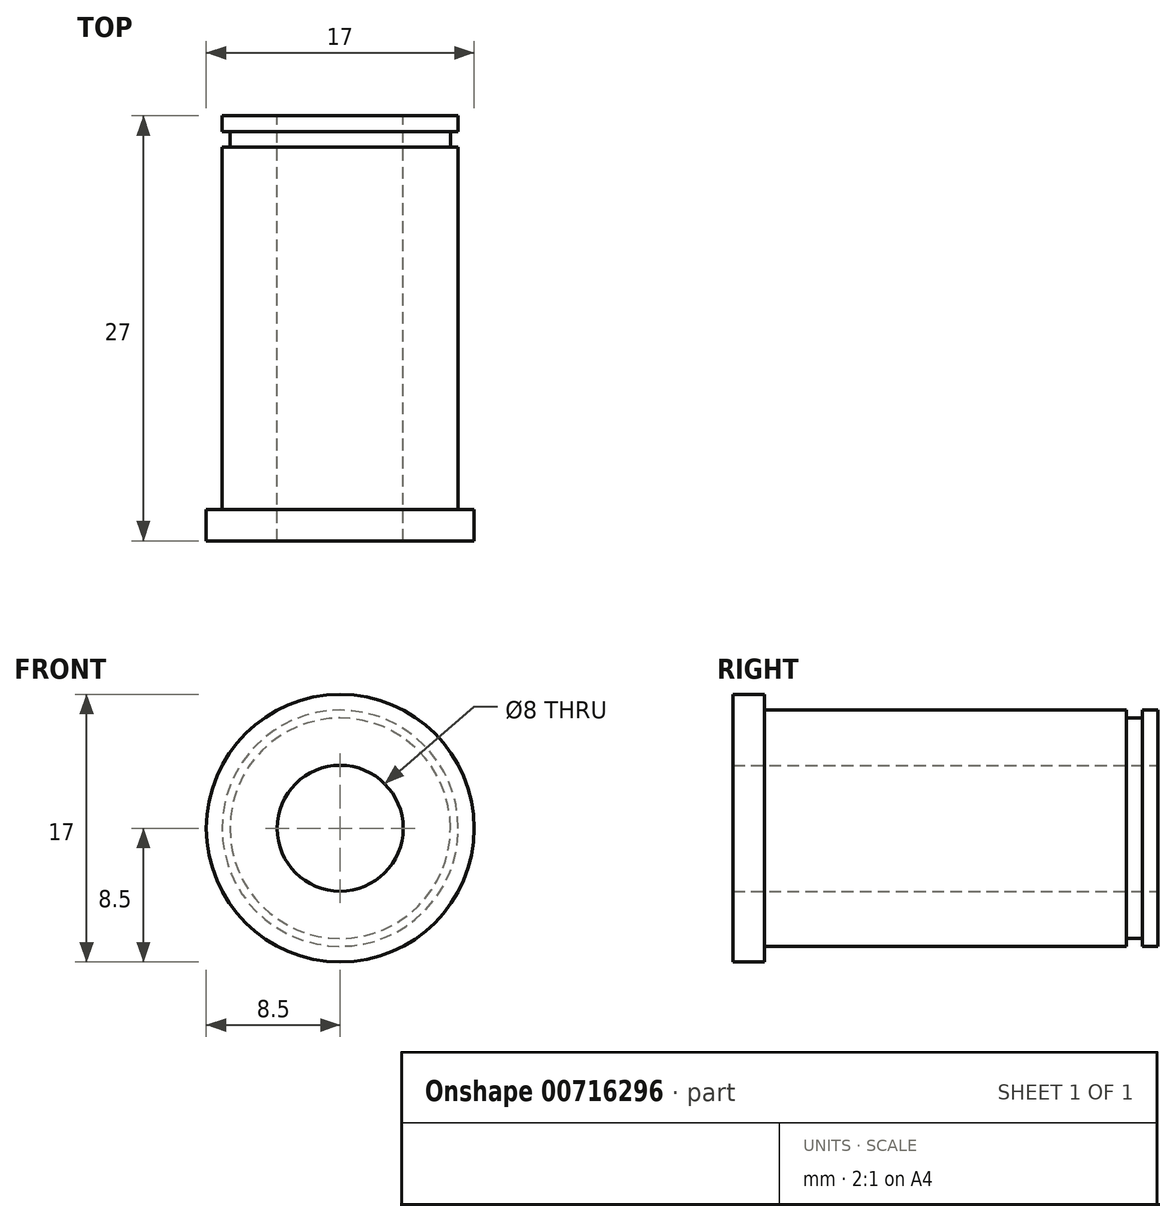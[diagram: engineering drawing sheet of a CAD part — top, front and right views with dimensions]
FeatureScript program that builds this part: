
annotation { "Feature Type Name" : "Feature", "Feature Type Description" : "" }
export const myFeature = defineFeature(function(context is Context, id is Id, definition is map)
    precondition{}
    {
        {
            var Q0;
            Q0=qCreatedBy(makeId("Front.planeOp"),FACE);
            var sketch = newSketch(context, id + "F0", { "sketchPlane" : qUnion([Q0])});
            skCircle(sketch, "E0", {"center": v(0, 0) * mm, "radius": 7.5 * mm});
            skCircle(sketch, "E1", {"center": v(0, 0) * mm, "radius": 8.5 * mm});
            skCircle(sketch, "E2", {"center": v(0, 0) * mm, "radius": 7 * mm});
            skCircle(sketch, "E3", {"center": v(0, 0) * mm, "radius": 4 * mm});
            skSolve(sketch);
        }
        {
            var Q0;
            Q0=makeQuery(id+"F0.imprint","IMPRINT",FACE,{"disambiguationData":[TD([[makeQuery(id+"F0.imprint","IMPRINT",EDGE,{"derivedFrom":sQuery(id+"F0.wireOp",EDGE,"E0")}),1.0]])]});
            var Q1;
            Q1=makeQuery(id+"F0.imprint","IMPRINT",FACE,{"disambiguationData":[TD([[makeQuery(id+"F0.imprint","IMPRINT",EDGE,{"derivedFrom":sQuery(id+"F0.wireOp",EDGE,"E2")}),1.0]])]});
            var Q2;
            Q2=makeQuery(id+"F0.imprint","IMPRINT",FACE,{"disambiguationData":[TD([[makeQuery(id+"F0.imprint","IMPRINT",EDGE,{"derivedFrom":sQuery(id+"F0.wireOp",EDGE,"E0")}),-1.0]])]});
            extrude(context, id + "F1", {"entities" : qUnion([Q0, Q1, Q2]), "depth" : 25 * mm, "offsetDistance" : 25 * mm});
        }
        {
            var Q0;
            Q0=makeQuery(id+"F0.imprint","IMPRINT",FACE,{"disambiguationData":[TD([[makeQuery(id+"F0.imprint","IMPRINT",EDGE,{"derivedFrom":sQuery(id+"F0.wireOp",EDGE,"E0")}),-1.0]])]});
            extrude(context, id + "F2", {"entities" : qUnion([Q0]), "operationType" : NewBodyOperationType.REMOVE, "oppositeDirection" : true, "depth" : -23 * mm, "offsetDistance" : 25 * mm});
        }
        {
            var Q0;
            Q0=makeQuery(id+"F0.imprint","IMPRINT",FACE,{"disambiguationData":[TD([[makeQuery(id+"F0.imprint","IMPRINT",EDGE,{"derivedFrom":sQuery(id+"F0.wireOp",EDGE,"E0")}),1.0]])]});
            var Q1;
            Q1=makeQuery(id+"F0.imprint","IMPRINT",FACE,{"disambiguationData":[TD([[makeQuery(id+"F0.imprint","IMPRINT",EDGE,{"derivedFrom":sQuery(id+"F0.wireOp",EDGE,"E2")}),1.0]])]});
            extrude(context, id + "F3", {"entities" : qUnion([Q0, Q1]), "operationType" : NewBodyOperationType.ADD, "depth" : -2 * mm, "offsetDistance" : 25 * mm});
        }
        {
            var Q0;
            Q0=makeQuery(id+"F0.imprint","IMPRINT",FACE,{"disambiguationData":[TD([[makeQuery(id+"F0.imprint","IMPRINT",EDGE,{"derivedFrom":sQuery(id+"F0.wireOp",EDGE,"E0")}),1.0]])]});
            extrude(context, id + "F4", {"entities" : qUnion([Q0]), "operationType" : NewBodyOperationType.REMOVE, "oppositeDirection" : true, "depth" : 1 * mm, "offsetDistance" : 25 * mm});
        }
    });
